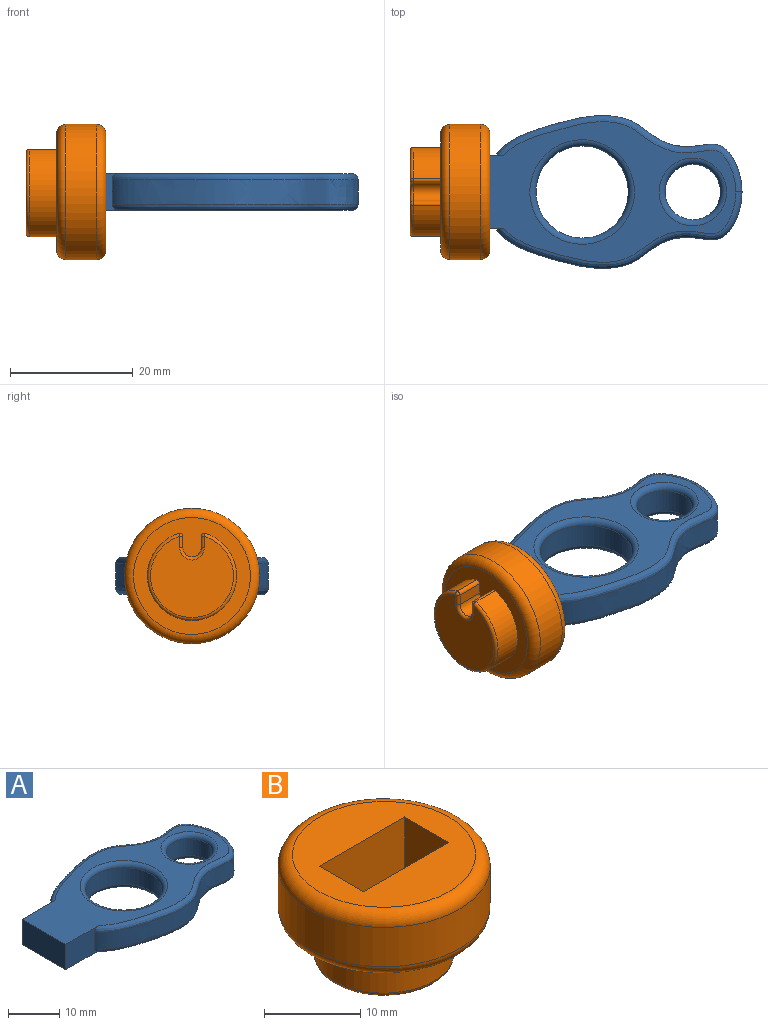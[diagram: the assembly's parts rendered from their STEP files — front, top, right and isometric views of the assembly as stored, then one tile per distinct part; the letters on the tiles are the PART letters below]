
ASSEMBLY  parts=2 mates=1
PART A: 17 faces, bbox 48.4x25.2x6.4 mm
  f0: plane 12x6mm, normal (-1,0,0), area 72mm2, adj f1,f6,f7,f8
  f1: plane 9.62x6.37mm, normal (0,-1,0), area 48.5mm2, adj f0,f2,f7,f8,f11,f15
  f2: extruded ~40x12.43mm, area 192.2mm2, adj f1,f3,f11,f15
  f3: extruded ~40x12.43mm, area 192.2mm2, adj f2,f6,f12,f16
  f4: cylinder r=4.5mm len=9mm, axis (0,0,-1), area 113.1mm2, adj f10,f14
  f5: cylinder r=7.5mm len=15mm, axis (0,0,-1), area 188.5mm2, adj f9,f13
  f6: plane 9.62x6.37mm, normal (0,1,0), area 48.5mm2, adj f0,f3,f7,f8,f12,f16
  f7: plane 47x22.86mm, normal (0,0,1), area 437.6mm2, adj f0,f1,f6,f13,f14,f15,f16
  f8: plane 47x22.86mm, normal (0,0,-1), area 437.6mm2, adj f0,f1,f6,f9,f10,f11,f12
  f9: torus R=8.5mm, axis (0,0,1), area 77.6mm2, adj f5,f8
  f10: torus R=5.5mm, axis (0,0,1), area 48mm2, adj f4,f8
  f11: bspline ~40.69x12.66mm, area 73.4mm2, adj f1,f2,f8,f12
  f12: bspline ~40.69x12.66mm, area 73.4mm2, adj f3,f6,f8,f11
  f13: torus R=8.5mm, axis (0,0,1), area 77.6mm2, adj f5,f7
  f14: torus R=5.5mm, axis (0,0,1), area 48mm2, adj f4,f7
  f15: bspline ~40.69x12.66mm, area 73.4mm2, adj f1,f2,f7,f16
  f16: bspline ~40.69x12.66mm, area 73.4mm2, adj f3,f6,f7,f15
PART B: 23 faces, bbox 23.8x23.8x13 mm
  f0: plane 19x19mm, normal (0,0,-1), area 129.9mm2, adj f8,f10,f11,f12,f13,f15,f17
  f1: plane 19x19mm, normal (0,0,1), area 202.3mm2, adj f3,f4,f5,f6,f9
  f2: cylinder r=11mm len=22mm, axis (0,0,-1), area 345.6mm2, adj f8,f9
  f3: plane 7x6.5mm, normal (-1,0,0), area 45.5mm2, adj f1,f4,f6,f7
  f4: plane 12.5x7mm, normal (0,-1,0), area 87.5mm2, adj f1,f3,f5,f7
  f5: plane 7x6.5mm, normal (1,0,0), area 45.5mm2, adj f1,f4,f6,f7
  f6: plane 12.5x7mm, normal (0,1,0), area 87.5mm2, adj f1,f3,f5,f7
  f7: plane 12.5x6.5mm, normal (0,0,1), area 81.2mm2, adj f3,f4,f5,f6
  f8: torus R=9.5mm, axis (0,0,1), area 154.8mm2, adj f0,f2
  f9: torus R=9.5mm, axis (0,0,1), area 154.8mm2, adj f1,f2
  f10: cylinder r=1.5mm len=4.5mm, axis (0,0,1), area 21.2mm2, adj f0,f11,f13,f21
  f11: plane 4.5x1.85mm, normal (1,0,0), area 8.3mm2, adj f0,f10,f17,f22
  f12: cylinder r=7.25mm len=14.5mm, axis (0,0,1), area 185.4mm2, adj f0,f15,f17,f18
  f13: plane 4.5x1.85mm, normal (-1,0,0), area 8.3mm2, adj f0,f10,f15,f19
  f14: plane 13.5x13.2mm, normal (0,0,-1), area 128.6mm2, adj f18,f19,f21,f22
  f15: cylinder r=0.5mm len=4.5mm, axis (0,0,1), area 4.2mm2, adj f0,f12,f13,f16
  f16: sphere r=0.5mm, area 0.5mm2, adj f15,f18,f19
  f17: cylinder r=0.5mm len=4.5mm, axis (0,0,1), area 4.2mm2, adj f0,f11,f12,f20
  f18: torus R=6.75mm, axis (0,0,1), area 31.5mm2, adj f12,f14,f16,f20
  f19: cylinder r=0.5mm len=1.85mm, axis (0,1,0), area 1.5mm2, adj f13,f14,f16,f21
  f20: sphere r=0.5mm, area 0.5mm2, adj f17,f18,f22
  f21: torus R=2mm, axis (0,0,1), area 4.1mm2, adj f10,f14,f19,f22
  f22: cylinder r=0.5mm len=1.85mm, axis (0,-1,0), area 1.5mm2, adj f11,f14,f20,f21
PLACE A t=(-0.33,3.78,14.88)mm fixed
PLACE B rot(axis=(0.58,0.58,0.58),120deg) t=(-1.33,3.78,17.88)mm
MATE fastened A.f0 <-> B.f2  axis (-1,0,0) through (-0.33,3.78,17.88)mm
